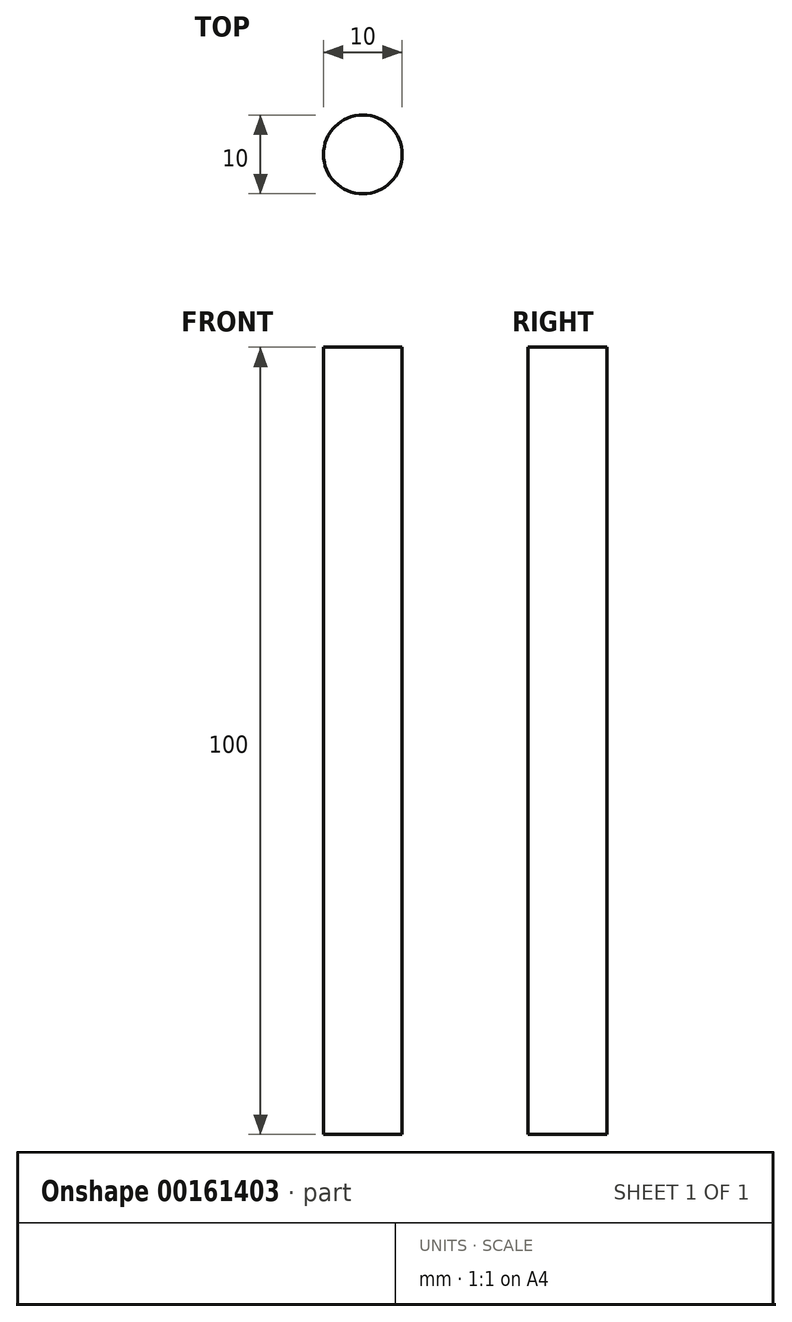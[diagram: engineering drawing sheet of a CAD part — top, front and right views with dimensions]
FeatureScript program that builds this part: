
annotation { "Feature Type Name" : "Feature", "Feature Type Description" : "" }
export const myFeature = defineFeature(function(context is Context, id is Id, definition is map)
    precondition{}
    {
        {
            var Q0;
            Q0=qCreatedBy(makeId("Top.planeOp"),FACE);
            var sketch = newSketch(context, id + "F0", { "sketchPlane" : qUnion([Q0])});
            skCircle(sketch, "E0", {"center": v(0, 0) * mm, "radius": 5 * mm});
            skSolve(sketch);
        }
        {
            var Q0;
            Q0=makeQuery(id+"F0.imprint","IMPRINT",FACE,{"disambiguationData":[TD([[makeQuery(id+"F0.imprint","IMPRINT",EDGE,{"derivedFrom":sQuery(id+"F0.wireOp",EDGE,"E0")}),1.0]])]});
            extrude(context, id + "F1", {"entities" : qUnion([Q0]), "depth" : 100 * mm});
        }
    });
